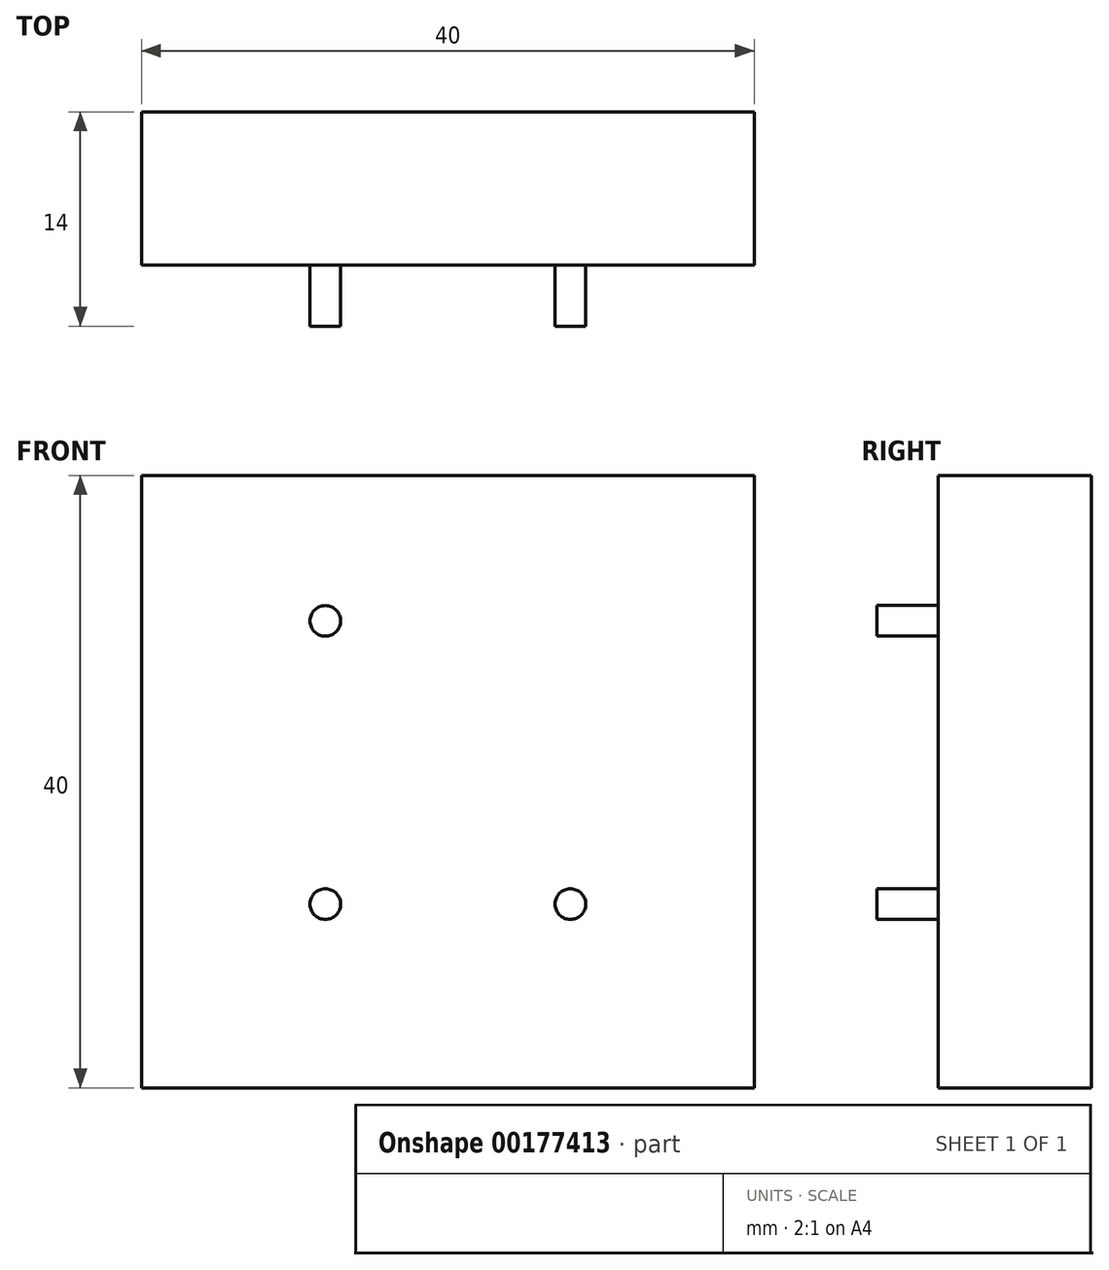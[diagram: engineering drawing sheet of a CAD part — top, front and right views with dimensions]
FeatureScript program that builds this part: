
annotation { "Feature Type Name" : "Feature", "Feature Type Description" : "" }
export const myFeature = defineFeature(function(context is Context, id is Id, definition is map)
    precondition{}
    {
        {
            var Q0;
            Q0=qCreatedBy(makeId("Right.planeOp"),FACE);
            var sketch = newSketch(context, id + "F0", { "sketchPlane" : qUnion([Q0])});
            skLineSegment(sketch, "E0.bottom", {"start": v(5, 20) * mm, "end": v(-5, 20) * mm});
            skLineSegment(sketch, "E0.top", {"start": v(5, -20) * mm, "end": v(-5, -20) * mm});
            skLineSegment(sketch, "E0.left", {"start": v(5, 20) * mm, "end": v(5, -20) * mm});
            skLineSegment(sketch, "E0.right", {"start": v(-5, 20) * mm, "end": v(-5, -20) * mm});
            skPoint(sketch, "E0.middle", {"position": v(0, 0) * mm});
            skSolve(sketch);
        }
        {
            var Q0;
            Q0 = qSketchRegion(id + "F0", true);
            extrude(context, id + "F1", {"entities" : qUnion([Q0]), "depth" : 20 * mm, "hasSecondDirection" : true, "secondDirectionOppositeDirection" : true, "secondDirectionDepth" : 20 * mm});
        }
        {
            var Q0;
            Q0=makeQuery(id+"F1.opExtrude","SWEPT_FACE",FACE,{"disambiguationData":[OSD([sQuery(id+"F0.wireOp",EDGE,"E0.right")])]});
            var sketch = newSketch(context, id + "F2", { "sketchPlane" : qUnion([Q0])});
            skCircle(sketch, "E1", {"center": v(-8, 10.5) * mm, "radius": 1 * mm});
            skCircle(sketch, "E2", {"center": v(-8, -8) * mm, "radius": 1 * mm});
            skCircle(sketch, "E3", {"center": v(8, -8) * mm, "radius": 1 * mm});
            skSolve(sketch);
        }
        {
            var Q0;
            Q0 = qSketchRegion(id + "F2", true);
            extrude(context, id + "F3", {"entities" : qUnion([Q0]), "operationType" : NewBodyOperationType.ADD, "depth" : 4 * mm});
        }
    });
